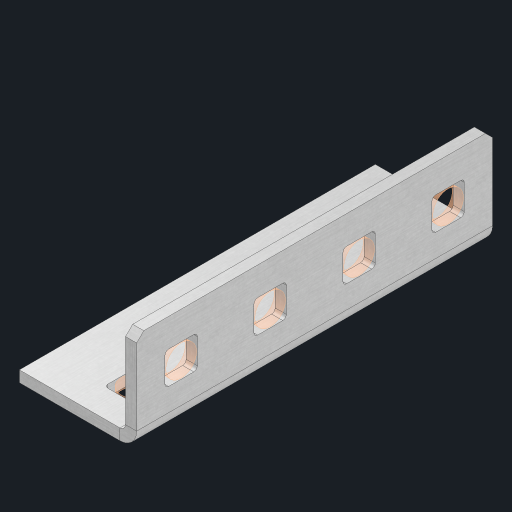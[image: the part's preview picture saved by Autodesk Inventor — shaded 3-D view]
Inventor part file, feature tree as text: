
AUTODESK INVENTOR PART (.ipt)
format: ipt  version: 2023 (Build 270158000, 158)  size: 478,720 bytes
history: native  units: in
note: dims shown in document units (in); Inventor stores cm internally (conversion verified against a paired STEP export)
features: other x13, sheet_metal_op x10, sketch x8, extrude x7, mirror x1, pattern_linear x1, chamfer x1
ambient origin geometry x8: Origin, YZ Plane, XZ Plane, XY Plane, X Axis, Y Axis, Z Axis, Center Point
bodies: Solid1 (feature_tree), Body (feature_tree)
feature tree (41):
  other  "Flange Pattern Plane"
  sheet_metal_op  "Flange Pattern"
  sheet_metal_op  "Body Pattern"
  other  "Arc Length"
  mirror  "Notch Mirror"
  pattern_linear  "Notch Pattern"  Spacing1=0.25in  [1 undecoded]
  chamfer  "End Chamfer"
  extrude  "Half Cut"  Depth=0.0625in
  sketch  "Sketch1"  dims[d0=1.5in]
  other  "Plate1"
  sketch  "Sketch2"  dims[d1=2.0in]
  other  "Plate2"
  sheet_metal_op  "Bend1"
  sheet_metal_op  "Corner1"
  sketch  "Sketch3"  dims[d2=0.0625in]
  other  "Flange Pattern Sketch"
  sketch  "Sketch7"  dims[d3=0.0625in]
  other  "Srf1"
  other  "Srf2"
  sketch  "Sketch8"  dims[d4=0.0312in]
  sketch  "Sketch9"  dims[d5=0.125in]
  other  "Srf91"
  sheet_metal_op  "Body Pattern Sketch"
  other  "Srf92"
  sketch  "Sketch13"  dims[d6=0.0625in]
  sketch  "Sketch14"  dims[d7=0.5in d8=90.0deg d9=0.0312in d10=0.25in d11=0.0625in d12=0.0625in d16=0.182in d17=0.02in d18=0.0625in d19=0.0in d20=0.25in d21=0.25in d46=0.172in d47=1.0in d48=0.0in d49=0.182in d50=0.02in d51=0.25in d52=0.25in d53=0.0625in d54=0.0in d55=0.172in d56=1.0in d57=0.0in d60=1.5748in d62=0.5in d63=0.3937in d65=0.5in d85=0.1473in d86=0.1782in d88=0.04in d89=0.0625in d90=0.0in d91=0.04in d92=0.0491in d95=2.5in d96=0.04in d97=0.25in d98=45.0deg d101=0.0in d102=2.497in d131=0.5in d132=1.5748in d134=0.5in d139=0.5in]
  other  "Srf856"
  other  "Srf1310"
  other  "Srf1311"
  other  "Srf1376"
  sheet_metal_op  "Flange Stamp"
  sheet_metal_op  "Flange Circle"
  sheet_metal_op  "Body Stamp"
  sheet_metal_op  "Body Circle"
  sheet_metal_op  "Notch"
  extrude  "ExtrusionSrf2"  Depth=0.0625in
  extrude  "ExtrusionSrf92"  Depth=0.182in
  extrude  "ExtrusionSrf856"  Depth=0.02in
  extrude  "ExtrusionSrf1310"  Depth=0.0625in
  extrude  "ExtrusionSrf1311"  TaperAngle=0.0deg  [1 undecoded]
  extrude  "ExtrusionSrf1376"  Depth=0.5in
note: 2 required parameter values undecoded (feature->parameter linkage not recoverable at this tier; creation-order binding heuristic only, values carry confidence <= 0.55)
